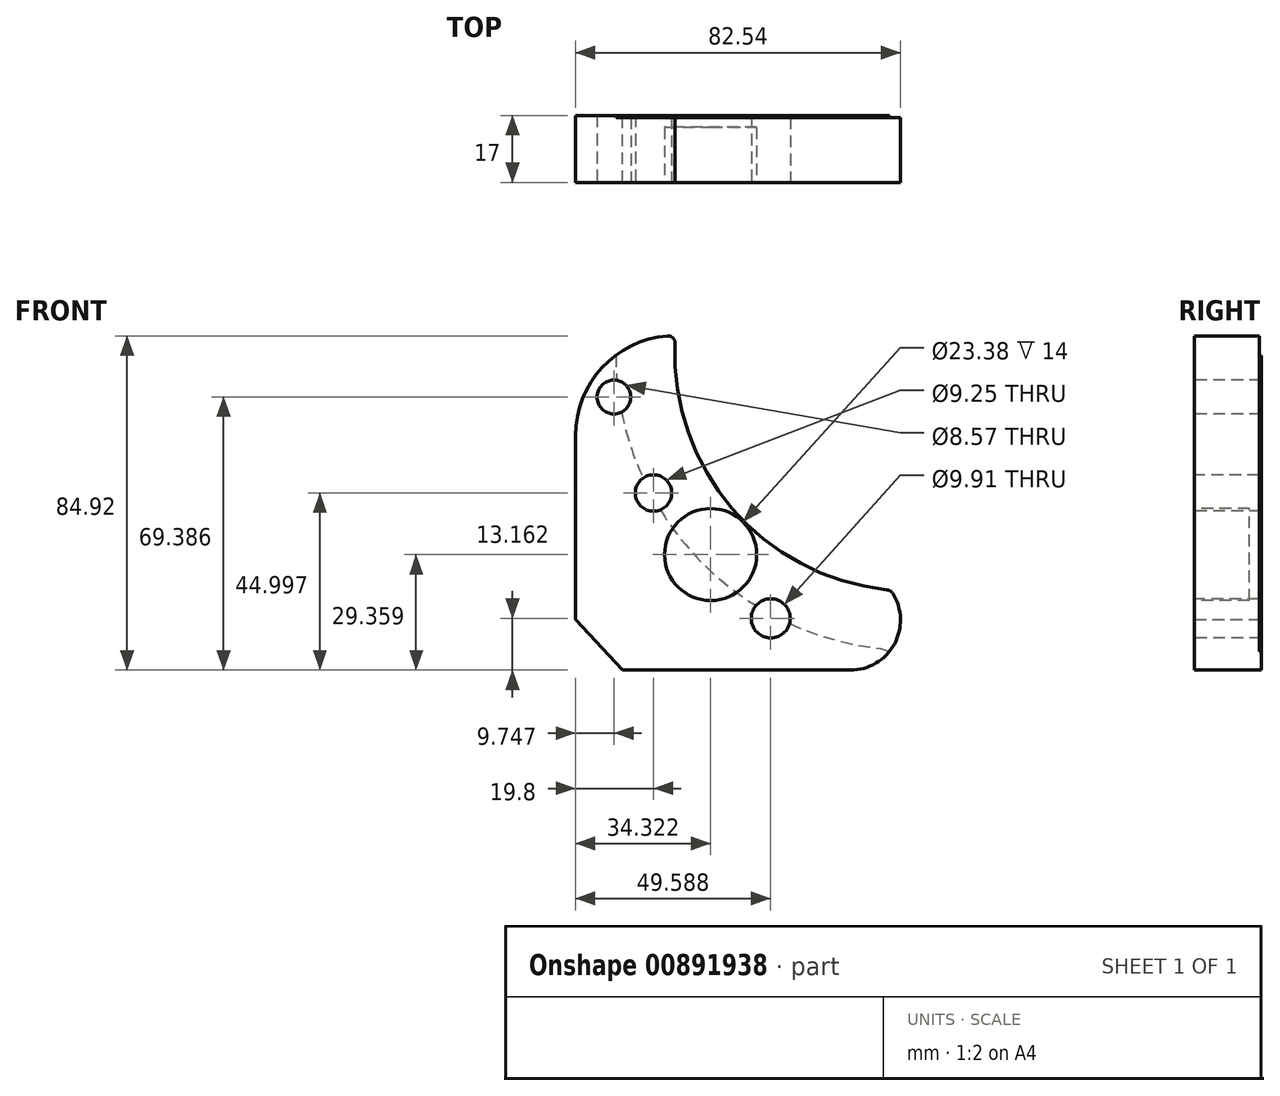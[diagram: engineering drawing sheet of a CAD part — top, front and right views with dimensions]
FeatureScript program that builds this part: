
annotation { "Feature Type Name" : "Feature", "Feature Type Description" : "" }
export const myFeature = defineFeature(function(context is Context, id is Id, definition is map)
    precondition{}
    {
        {
            var Q0;
            Q0=qCreatedBy(makeId("Front.planeOp"),FACE);
            var sketch = newSketch(context, id + "F0", { "sketchPlane" : qUnion([Q0])});
            skLineSegment(sketch, "E0.top", {"start": v(-28.08, -40.25) * mm, "end": v(29.84, -40.25) * mm});
            skPoint(sketch, "E1.visualSharp", {"position": v(-40, 44.75) * mm});
            skArc(sketch, "E1.filletArc", {"start": v(-16.65, 44.67) * mm, "mid": v(-33.27, 36.57) * mm, "end": v(-40, 19.35) * mm});
            skPoint(sketch, "E2.visualSharp", {"position": v(40, -40.25) * mm});
            skArc(sketch, "E2.filletArc", {"start": v(29.84, -40.25) * mm, "mid": v(40.96, -33.68) * mm, "end": v(40.58, -20.77) * mm});
            skArc(sketch, "E3", {"start": v(-14.72, 42.8) * mm, "mid": v(-0.21, 0.84) * mm, "end": v(39.08, -19.84) * mm});
            skLineSegment(sketch, "E4", {"start": v(-40, -27.43) * mm, "end": v(-28.08, -40.25) * mm});
            skLineSegment(sketch, "E5", {"start": v(-40, 19.35) * mm, "end": v(-40, -27.43) * mm});
            skPoint(sketch, "E6.visualSharp", {"position": v(-14.6, 44.75) * mm});
            skArc(sketch, "E6.filletArc", {"start": v(-14.72, 42.8) * mm, "mid": v(-15.26, 44.17) * mm, "end": v(-16.65, 44.67) * mm});
            skPoint(sketch, "E7.visualSharp", {"position": v(40, -19.93) * mm});
            skArc(sketch, "E7.filletArc", {"start": v(40.58, -20.77) * mm, "mid": v(39.94, -20.13) * mm, "end": v(39.08, -19.84) * mm});
            skSolve(sketch);
        }
        {
            var Q0;
            Q0=makeQuery(id+"F0.imprint","IMPRINT",FACE,{"disambiguationData":[TD([[makeQuery(id+"F0.imprint","IMPRINT",EDGE,{"derivedFrom":sQuery(id+"F0.wireOp",EDGE,"E0.top")}),1.0]])]});
            extrude(context, id + "F1", {"entities" : qUnion([Q0]), "depth" : 17 * mm, "offsetDistance" : 25.4 * mm});
        }
        {
            var Q0;
            Q0=makeQuery(id+"F1.opExtrude","CAP_FACE",FACE,{"disambiguationData":[OSD([sQuery(id+"F0.wireOp",EDGE,"E0.top"),sQuery(id+"F0.wireOp",EDGE,"E1.filletArc"),sQuery(id+"F0.wireOp",EDGE,"E2.filletArc"),sQuery(id+"F0.wireOp",EDGE,"E3"),sQuery(id+"F0.wireOp",EDGE,"E4"),sQuery(id+"F0.wireOp",EDGE,"E5"),sQuery(id+"F0.wireOp",EDGE,"E6.filletArc"),sQuery(id+"F0.wireOp",EDGE,"E7.filletArc")])],"isStart":false});
            var sketch = newSketch(context, id + "F2", { "sketchPlane" : qUnion([Q0])});
            skCircle(sketch, "E8", {"center": v(-5.68, -10.9) * mm, "radius": 11.7 * mm});
            skSolve(sketch);
        }
        {
            var Q0;
            Q0 = qSketchRegion(id + "F2", true);
            extrude(context, id + "F3", {"entities" : qUnion([Q0]), "operationType" : NewBodyOperationType.REMOVE, "oppositeDirection" : true, "depth" : 14 * mm, "offsetDistance" : 25 * mm});
        }
        {
            var Q0;
            Q0=makeQuery(id+"F1.opExtrude","CAP_FACE",FACE,{"disambiguationData":[OSD([sQuery(id+"F0.wireOp",EDGE,"E0.top"),sQuery(id+"F0.wireOp",EDGE,"E1.filletArc"),sQuery(id+"F0.wireOp",EDGE,"E2.filletArc"),sQuery(id+"F0.wireOp",EDGE,"E3"),sQuery(id+"F0.wireOp",EDGE,"E4"),sQuery(id+"F0.wireOp",EDGE,"E5"),sQuery(id+"F0.wireOp",EDGE,"E6.filletArc"),sQuery(id+"F0.wireOp",EDGE,"E7.filletArc")])],"isStart":false});
            var sketch = newSketch(context, id + "F4", { "sketchPlane" : qUnion([Q0])});
            skCircle(sketch, "E9", {"center": v(-20.2, 4.75) * mm, "radius": 4.62 * mm});
            skCircle(sketch, "E10", {"center": v(-30.25, 29.14) * mm, "radius": 4.29 * mm});
            skCircle(sketch, "E11", {"center": v(9.59, -27.09) * mm, "radius": 4.96 * mm});
            skSolve(sketch);
        }
        {
            var Q0;
            Q0 = qSketchRegion(id + "F4", true);
            extrude(context, id + "F5", {"entities" : qUnion([Q0]), "operationType" : NewBodyOperationType.REMOVE, "oppositeDirection" : true, "depth" : 25 * mm, "offsetDistance" : 25 * mm});
        }
        {
            var Q0;
            Q0=makeQuery(id+"F1.opExtrude","CAP_FACE",FACE,{"disambiguationData":[OSD([sQuery(id+"F0.wireOp",EDGE,"E0.top"),sQuery(id+"F0.wireOp",EDGE,"E1.filletArc"),sQuery(id+"F0.wireOp",EDGE,"E2.filletArc"),sQuery(id+"F0.wireOp",EDGE,"E3"),sQuery(id+"F0.wireOp",EDGE,"E4"),sQuery(id+"F0.wireOp",EDGE,"E5"),sQuery(id+"F0.wireOp",EDGE,"E6.filletArc"),sQuery(id+"F0.wireOp",EDGE,"E7.filletArc")])],"isStart":true});
            var sketch = newSketch(context, id + "F6", { "sketchPlane" : qUnion([Q0])});
            skArc(sketch, "E12.0", {"start": v(29.77, 39.7) * mm, "mid": v(10.35, -10.35) * mm, "end": v(-37.47, -34.75) * mm});
            skArc(sketch, "E13.0", {"start": v(9.72, 42.58) * mm, "mid": v(-3.58, 4.1) * mm, "end": v(-39.62, -14.87) * mm});
            skArc(sketch, "E14.0", {"start": v(-44.81, -37) * mm, "mid": v(-47.54, -27.55) * mm, "end": v(-44.81, -18.1) * mm});
            skArc(sketch, "E15.0", {"start": v(17.06, 49.65) * mm, "mid": v(23.64, 48.38) * mm, "end": v(29.77, 45.7) * mm});
            skLineSegment(sketch, "E16", {"start": v(17.06, 49.65) * mm, "end": v(9.72, 42.58) * mm});
            skLineSegment(sketch, "E17", {"start": v(-39.62, -14.87) * mm, "end": v(-44.81, -18.1) * mm});
            skLineSegment(sketch, "E18", {"start": v(-37.47, -34.75) * mm, "end": v(-44.81, -37) * mm});
            skLineSegment(sketch, "E19", {"start": v(29.77, 39.7) * mm, "end": v(29.77, 45.7) * mm});
            skSolve(sketch);
        }
        {
            var Q0;
            Q0 = qSketchRegion(id + "F6", true);
            extrude(context, id + "F7", {"entities" : qUnion([Q0]), "operationType" : NewBodyOperationType.REMOVE, "oppositeDirection" : true, "depth" : 0.5 * mm, "offsetDistance" : 25 * mm});
        }
    });
